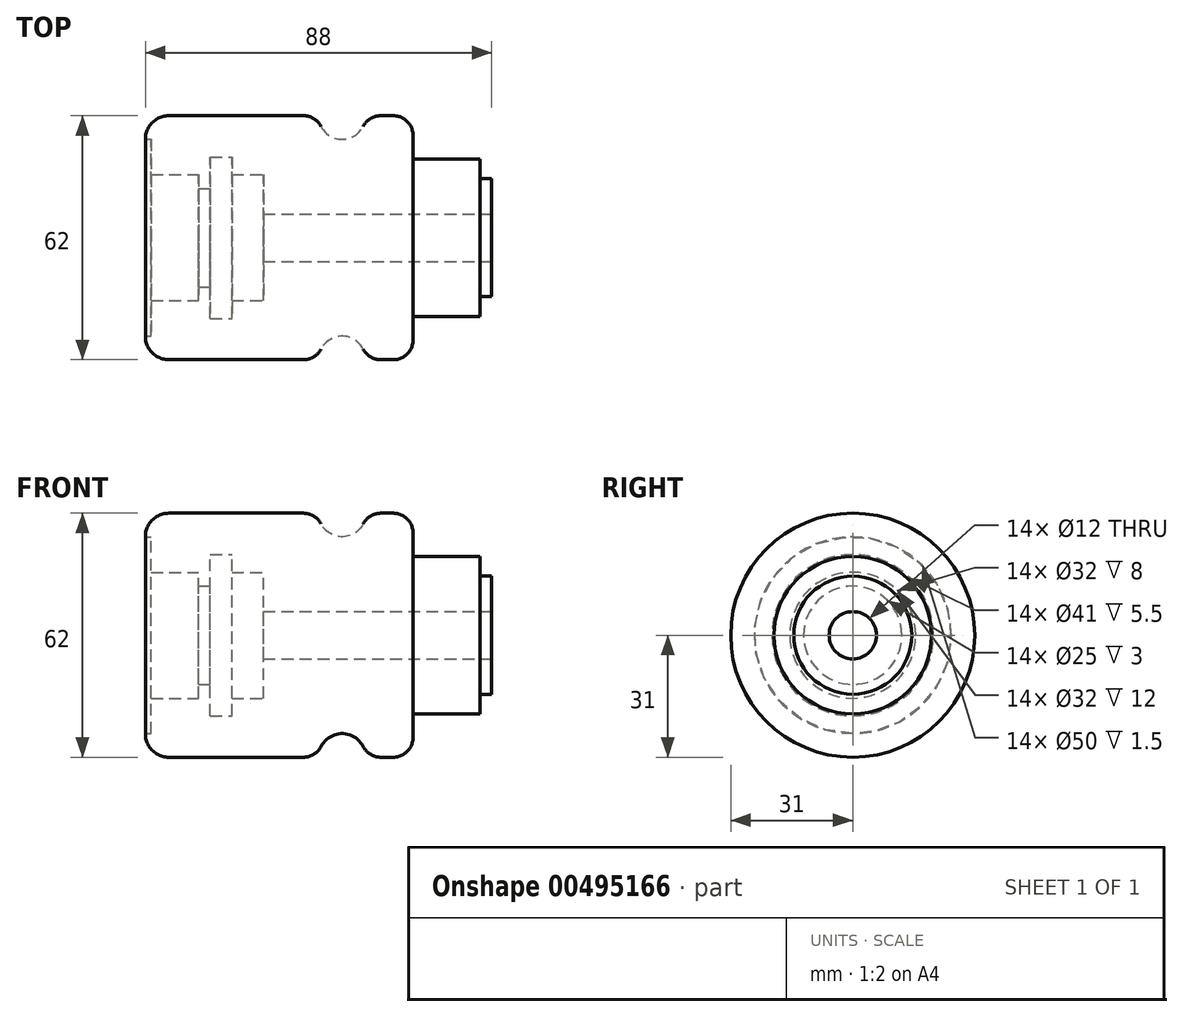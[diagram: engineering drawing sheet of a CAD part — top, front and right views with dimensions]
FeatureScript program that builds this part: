
annotation { "Feature Type Name" : "Feature", "Feature Type Description" : "" }
export const myFeature = defineFeature(function(context is Context, id is Id, definition is map)
    precondition{}
    {
        {
            var Q0;
            Q0=qCreatedBy(makeId("Front.planeOp"),FACE);
            var sketch = newSketch(context, id + "F0", { "sketchPlane" : qUnion([Q0])});
            skLineSegment(sketch, "E0", {"start": v(0, 0) * mm, "end": v(74.32, 0) * mm, "construction": true});
            skLineSegment(sketch, "E1", {"start": v(0, 0) * mm, "end": v(0, 31) * mm});
            skLineSegment(sketch, "E2", {"start": v(0, 31) * mm, "end": v(44, 31) * mm});
            skLineSegment(sketch, "E3", {"start": v(68, 31) * mm, "end": v(68, 20) * mm});
            skLineSegment(sketch, "E4", {"start": v(68, 20) * mm, "end": v(85, 20) * mm});
            skLineSegment(sketch, "E5", {"start": v(85, 20) * mm, "end": v(85, 15) * mm});
            skLineSegment(sketch, "E6", {"start": v(85, 15) * mm, "end": v(88, 15) * mm});
            skLineSegment(sketch, "E7", {"start": v(88, 15) * mm, "end": v(88, 0) * mm});
            skLineSegment(sketch, "E8", {"start": v(88, 0) * mm, "end": v(0, 0) * mm});
            skArc(sketch, "E9", {"start": v(44, 31) * mm, "mid": v(50, 25) * mm, "end": v(56, 31) * mm});
            skLineSegment(sketch, "E10.trimOffspring", {"start": v(56, 31) * mm, "end": v(68, 31) * mm});
            skSolve(sketch);
        }
        {
            var Q0;
            Q0 = qSketchRegion(id + "F0", true);
            var Q1;
            Q1=sQuery(id+"F0.wireOp",EDGE,"E8");
            revolve(context, id + "F1", {"entities" : qUnion([Q0]), "axis" : qUnion([Q1]), "revolveType" : RevolveType.FULL});
        }
        {
            var Q0;
            Q0=qCreatedBy(makeId("Front.planeOp"),FACE);
            var sketch = newSketch(context, id + "F2", { "sketchPlane" : qUnion([Q0])});
            skLineSegment(sketch, "E11", {"start": v(0, 0) * mm, "end": v(0, 25) * mm});
            skLineSegment(sketch, "E12", {"start": v(0, 25) * mm, "end": v(1.5, 25) * mm});
            skLineSegment(sketch, "E13", {"start": v(1.5, 25) * mm, "end": v(1.5, 16) * mm});
            skLineSegment(sketch, "E14", {"start": v(1.5, 16) * mm, "end": v(13.5, 16) * mm});
            skLineSegment(sketch, "E15", {"start": v(13.5, 16) * mm, "end": v(13.5, 12.5) * mm});
            skLineSegment(sketch, "E16", {"start": v(13.5, 12.5) * mm, "end": v(16.5, 12.5) * mm});
            skLineSegment(sketch, "E17", {"start": v(16.5, 12.5) * mm, "end": v(16.5, 20.5) * mm});
            skLineSegment(sketch, "E18", {"start": v(16.5, 20.5) * mm, "end": v(22, 20.5) * mm});
            skLineSegment(sketch, "E19", {"start": v(22, 20.5) * mm, "end": v(22, 16) * mm});
            skLineSegment(sketch, "E20", {"start": v(22, 16) * mm, "end": v(30, 16) * mm});
            skLineSegment(sketch, "E21", {"start": v(30, 16) * mm, "end": v(30, 6) * mm});
            skLineSegment(sketch, "E22", {"start": v(30, 6) * mm, "end": v(88, 6) * mm});
            skLineSegment(sketch, "E23", {"start": v(88, 6) * mm, "end": v(88, 0) * mm});
            skLineSegment(sketch, "E24", {"start": v(88, 0) * mm, "end": v(0, 0) * mm});
            skLineSegment(sketch, "E25", {"start": v(0, 0) * mm, "end": v(-16.98, 0) * mm, "construction": true});
            skLineSegment(sketch, "E26", {"start": v(-16.98, 0) * mm, "end": v(106.75, 0) * mm, "construction": true});
            skSolve(sketch);
        }
        {
            var Q0;
            Q0 = qSketchRegion(id + "F2", true);
            var Q1;
            Q1=sQuery(id+"F2.wireOp",EDGE,"E26");
            revolve(context, id + "F3", {"operationType" : NewBodyOperationType.REMOVE, "entities" : qUnion([Q0]), "axis" : qUnion([Q1]), "revolveType" : RevolveType.FULL, "oppositeDirection" : true});
        }
        {
            var Q0;
            Q0=makeQuery(id+"F1.opRevolve","SWEPT_EDGE",EDGE,{"disambiguationData":[OSD([sQuery(id+"F0.wireOp",EDGE,"E1"),sQuery(id+"F0.wireOp",EDGE,"E2")])]});
            fillet(context, id + "F4", {"entities" : qUnion([Q0]), "radius" : 6 * mm, "tangentPropagation" : true, "allowEdgeOverflow" : false});
        }
        {
            var Q0;
            Q0=makeQuery(id+"F1.opRevolve","SWEPT_EDGE",EDGE,{"disambiguationData":[OSD([sQuery(id+"F0.wireOp",EDGE,"E2"),sQuery(id+"F0.wireOp",EDGE,"E9")])]});
            var Q1;
            Q1=makeQuery(id+"F1.opRevolve","SWEPT_EDGE",EDGE,{"disambiguationData":[OSD([sQuery(id+"F0.wireOp",EDGE,"E9"),sQuery(id+"F0.wireOp",EDGE,"E10.trimOffspring")])]});
            fillet(context, id + "F5", {"entities" : qUnion([Q0, Q1]), "radius" : 5 * mm, "tangentPropagation" : true, "allowEdgeOverflow" : false});
        }
        {
            var Q0;
            Q0=makeQuery(id+"F1.opRevolve","SWEPT_EDGE",EDGE,{"disambiguationData":[OSD([sQuery(id+"F0.wireOp",EDGE,"E3"),sQuery(id+"F0.wireOp",EDGE,"E10.trimOffspring")])]});
            fillet(context, id + "F6", {"entities" : qUnion([Q0]), "radius" : 5 * mm, "tangentPropagation" : true, "allowEdgeOverflow" : false});
        }
    });
